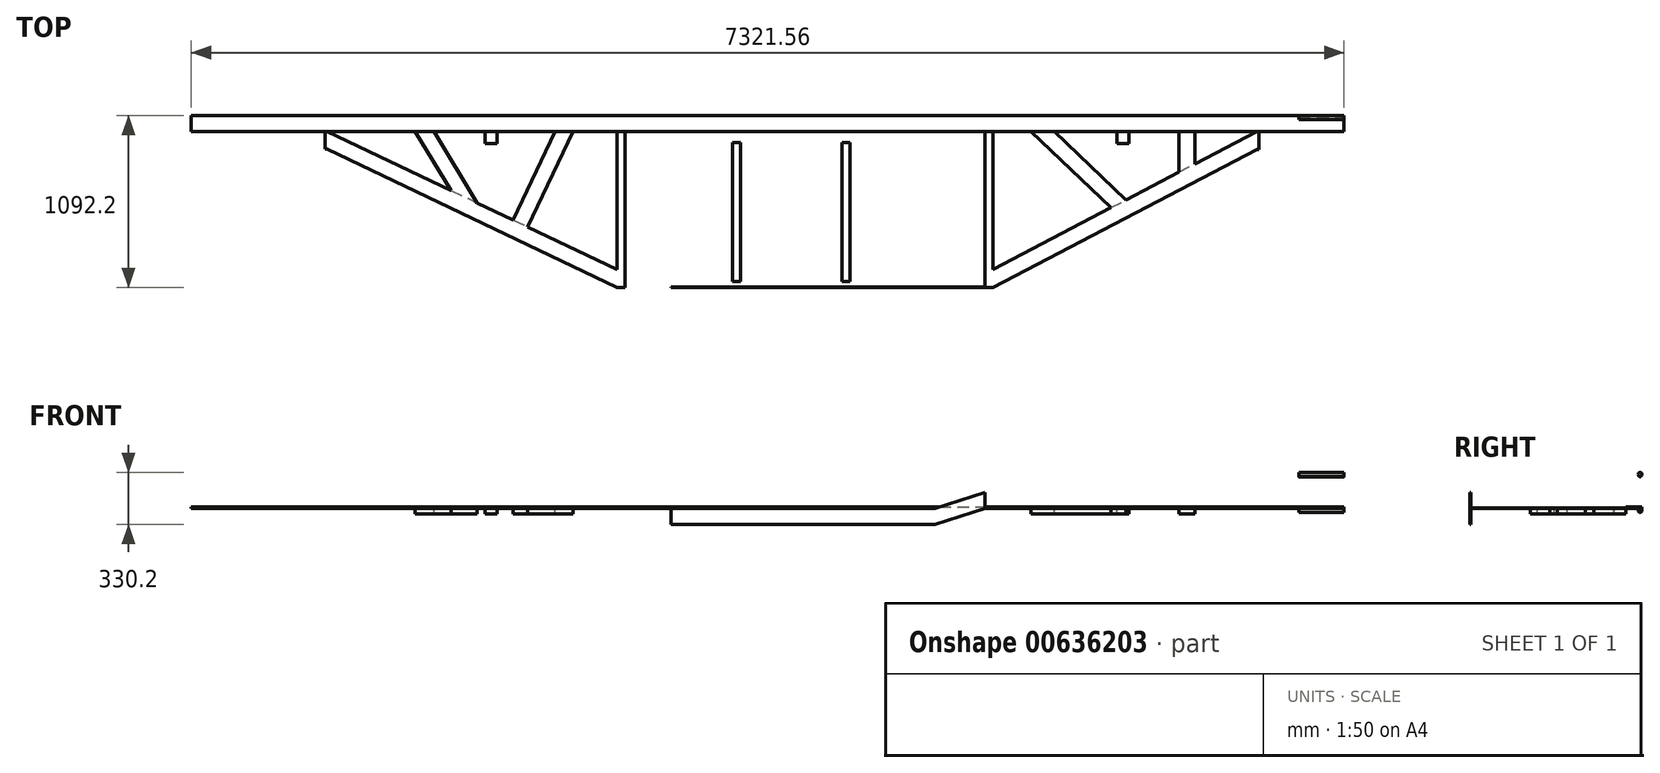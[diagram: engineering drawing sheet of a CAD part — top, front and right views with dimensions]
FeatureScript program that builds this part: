
annotation { "Feature Type Name" : "Feature", "Feature Type Description" : "" }
export const myFeature = defineFeature(function(context is Context, id is Id, definition is map)
    precondition{}
    {
        {
            assignVariable(context, id + "F0", {"name" : "MainRailLength", "anyValue" : 288.25});
        }
        {
            assignVariable(context, id + "F1", {"name" : "MainRailHeight", "anyValue" : 8});
        }
        {
            assignVariable(context, id + "F2", {"name" : "SideRailHeight", "anyValue" : 4});
        }
        {
            assignVariable(context, id + "F3", {"name" : "SideRailWidth", "anyValue" : 4});
        }
        {
            assignVariable(context, id + "F4", {"name" : "BunkRailHeight", "anyValue" : 4});
        }
        {
            var Q0;
            Q0=qCreatedBy(makeId("Top.planeOp"),FACE);
            var sketch = newSketch(context, id + "F5", { "sketchPlane" : qUnion([Q0])});
            skLineSegment(sketch, "E0.bottom", {"start": v(-3660.78, 0) * mm, "end": v(3660.78, 0) * mm});
            skLineSegment(sketch, "E0.top", {"start": v(-3660.78, -101.6) * mm, "end": v(3660.78, -101.6) * mm});
            skLineSegment(sketch, "E0.left", {"start": v(-3660.78, 0) * mm, "end": v(-3660.78, -101.6) * mm});
            skLineSegment(sketch, "E0.right", {"start": v(3660.78, 0) * mm, "end": v(3660.78, -101.6) * mm});
            skSolve(sketch);
        }
        {
            var Q0;
            Q0=makeQuery(id+"F5.imprint","IMPRINT",FACE,{"disambiguationData":[TD([[makeQuery(id+"F5.imprint","IMPRINT",EDGE,{"derivedFrom":sQuery(id+"F5.wireOp",EDGE,"E0.bottom")}),-1.0]])]});
            extrude(context, id + "F6", {"entities" : qUnion([Q0]), "depth" : (getVariable(context, 'MainRailHeight')) * mm, "offsetDistance" : 25.4 * mm});
        }
        {
            var Q0;
            Q0=makeQuery(id+"F6.opExtrude","SWEPT_FACE",FACE,{"disambiguationData":[OSD([sQuery(id+"F5.wireOp",EDGE,"E0.right")])]});
            var sketch = newSketch(context, id + "F7", { "sketchPlane" : qUnion([Q0])});
            skCircle(sketch, "E1", {"center": v(-12.7, 215.9) * mm, "radius": 12.7 * mm});
            skPoint(sketch, "E1.centerSnap0", {"position": v(-50.8, 203.2) * mm});
            skCircle(sketch, "E2", {"center": v(-12.7, -12.7) * mm, "radius": 12.7 * mm});
            skCircle(sketch, "E3", {"center": v(-12.7, 203.2) * mm, "radius": 3.18 * mm});
            skCircle(sketch, "E4", {"center": v(-12.7, 0) * mm, "radius": 3.18 * mm});
            skSolve(sketch);
        }
        {
            var Q0;
            {var subQ0=sQuery(id+"F7.wireOp",EDGE,"E3");var subQ1=sQuery(id+"F7.wireOp",EDGE,"E1");var subQ2=makeQuery(id+"F7.imprint","INTERSECT",VERTEX,{"disambiguationData":[OD(0.0)],"derivedFrom":[subQ1,subQ0]});Q0=makeQuery(id+"F7.imprint","IMPRINT",FACE,{"disambiguationData":[TD([[makeQuery(id+"F7.imprint","IMPRINT",EDGE,{"disambiguationData":[TD([[subQ2,1.0]])],"derivedFrom":subQ1}),1.0]])]});}
            var Q1;
            {var subQ0=sQuery(id+"F7.wireOp",EDGE,"E3");var subQ1=sQuery(id+"F7.wireOp",EDGE,"E1");var subQ2=makeQuery(id+"F7.imprint","INTERSECT",VERTEX,{"disambiguationData":[OD(0.0)],"derivedFrom":[subQ1,subQ0]});Q1=makeQuery(id+"F7.imprint","IMPRINT",FACE,{"disambiguationData":[TD([[makeQuery(id+"F7.imprint","IMPRINT",EDGE,{"disambiguationData":[TD([[subQ2,-1.0]])],"derivedFrom":subQ1}),-1.0]])]});}
            var Q2;
            {var subQ0=sQuery(id+"F7.wireOp",EDGE,"E3");var subQ1=sQuery(id+"F7.wireOp",EDGE,"E1");var subQ2=makeQuery(id+"F7.imprint","INTERSECT",VERTEX,{"disambiguationData":[OD(1.0)],"derivedFrom":[subQ1,subQ0]});Q2=makeQuery(id+"F7.imprint","IMPRINT",FACE,{"disambiguationData":[TD([[makeQuery(id+"F7.imprint","IMPRINT",EDGE,{"disambiguationData":[TD([[subQ2,1.0]])],"derivedFrom":subQ1}),-1.0]])]});}
            var Q3;
            {var subQ0=sQuery(id+"F7.wireOp",EDGE,"E3");var subQ1=makeQuery(id+"F6.opExtrude","CAP_EDGE",EDGE,{"disambiguationData":[OSD([sQuery(id+"F5.wireOp",EDGE,"E0.right")])],"isStart":false});var subQ2=makeQuery(id+"F7.imprint","INTERSECT",VERTEX,{"disambiguationData":[OD(0.0)],"derivedFrom":[subQ1,subQ0]});Q3=makeQuery(id+"F7.imprint","IMPRINT",FACE,{"disambiguationData":[TD([[makeQuery(id+"F7.imprint","IMPRINT",EDGE,{"disambiguationData":[TD([[subQ2,1.0]])],"derivedFrom":subQ0}),1.0]])]});}
            var Q4;
            {var subQ0=sQuery(id+"F7.wireOp",EDGE,"E3");var subQ1=sQuery(id+"F7.wireOp",EDGE,"E1");var subQ2=makeQuery(id+"F7.imprint","INTERSECT",VERTEX,{"disambiguationData":[OD(0.0)],"derivedFrom":[subQ1,subQ0]});Q4=makeQuery(id+"F7.imprint","IMPRINT",FACE,{"disambiguationData":[TD([[makeQuery(id+"F7.imprint","IMPRINT",EDGE,{"disambiguationData":[TD([[subQ2,-1.0]])],"derivedFrom":subQ1}),1.0]])]});}
            var Q5;
            {var subQ0=sQuery(id+"F7.wireOp",EDGE,"E4");var subQ1=sQuery(id+"F7.wireOp",EDGE,"E2");var subQ2=makeQuery(id+"F7.imprint","INTERSECT",VERTEX,{"disambiguationData":[OD(0.0)],"derivedFrom":[subQ1,subQ0]});Q5=makeQuery(id+"F7.imprint","IMPRINT",FACE,{"disambiguationData":[TD([[makeQuery(id+"F7.imprint","IMPRINT",EDGE,{"disambiguationData":[TD([[subQ2,1.0]])],"derivedFrom":subQ1}),1.0]])]});}
            var Q6;
            {var subQ0=sQuery(id+"F7.wireOp",EDGE,"E4");var subQ1=sQuery(id+"F7.wireOp",EDGE,"E2");var subQ2=makeQuery(id+"F7.imprint","INTERSECT",VERTEX,{"disambiguationData":[OD(0.0)],"derivedFrom":[subQ1,subQ0]});Q6=makeQuery(id+"F7.imprint","IMPRINT",FACE,{"disambiguationData":[TD([[makeQuery(id+"F7.imprint","IMPRINT",EDGE,{"disambiguationData":[TD([[subQ2,-1.0]])],"derivedFrom":subQ1}),1.0]])]});}
            var Q7;
            {var subQ0=sQuery(id+"F7.wireOp",EDGE,"E4");var subQ1=sQuery(id+"F7.wireOp",EDGE,"E2");var subQ2=makeQuery(id+"F7.imprint","INTERSECT",VERTEX,{"disambiguationData":[OD(1.0)],"derivedFrom":[subQ1,subQ0]});Q7=makeQuery(id+"F7.imprint","IMPRINT",FACE,{"disambiguationData":[TD([[makeQuery(id+"F7.imprint","IMPRINT",EDGE,{"disambiguationData":[TD([[subQ2,1.0]])],"derivedFrom":subQ1}),-1.0]])]});}
            var Q8;
            {var subQ0=sQuery(id+"F7.wireOp",EDGE,"E4");var subQ1=sQuery(id+"F7.wireOp",EDGE,"E2");var subQ2=makeQuery(id+"F7.imprint","INTERSECT",VERTEX,{"disambiguationData":[OD(0.0)],"derivedFrom":[subQ1,subQ0]});Q8=makeQuery(id+"F7.imprint","IMPRINT",FACE,{"disambiguationData":[TD([[makeQuery(id+"F7.imprint","IMPRINT",EDGE,{"disambiguationData":[TD([[subQ2,-1.0]])],"derivedFrom":subQ1}),-1.0]])]});}
            extrude(context, id + "F8", {"entities" : qUnion([Q0, Q1, Q2, Q3, Q4, Q5, Q6, Q7, Q8]), "operationType" : NewBodyOperationType.ADD, "oppositeDirection" : true, "depth" : (getVariable(context, 'MainRailLength')) * mm, "offsetDistance" : 25.4 * mm});
        }
        {
            var Q0;
            Q0=qCreatedBy(makeId("Top.planeOp"),FACE);
            var sketch = newSketch(context, id + "F9", { "sketchPlane" : qUnion([Q0])});
            skLineSegment(sketch, "E5.bottom", {"start": v(-955.67, -101.6) * mm, "end": v(-904.87, -101.6) * mm});
            skLineSegment(sketch, "E5.top", {"start": v(-955.67, -1092.2) * mm, "end": v(-904.87, -1092.2) * mm});
            skLineSegment(sketch, "E5.left", {"start": v(-955.67, -101.6) * mm, "end": v(-955.67, -1092.2) * mm});
            skLineSegment(sketch, "E5.right", {"start": v(-904.87, -101.6) * mm, "end": v(-904.87, -1092.2) * mm});
            skLineSegment(sketch, "E6.bottom", {"start": v(1381.12, -101.6) * mm, "end": v(1431.92, -101.6) * mm});
            skLineSegment(sketch, "E6.top", {"start": v(1381.12, -1092.2) * mm, "end": v(1431.93, -1092.2) * mm});
            skLineSegment(sketch, "E6.left", {"start": v(1381.12, -101.6) * mm, "end": v(1381.12, -1092.2) * mm});
            skLineSegment(sketch, "E6.right", {"start": v(1431.92, -101.6) * mm, "end": v(1431.92, -1092.2) * mm});
            skSolve(sketch);
        }
        {
            var Q0;
            Q0=makeQuery(id+"F9.imprint","IMPRINT",FACE,{"disambiguationData":[TD([[makeQuery(id+"F9.imprint","IMPRINT",EDGE,{"derivedFrom":sQuery(id+"F9.wireOp",EDGE,"E5.bottom")}),-1.0]])]});
            var Q1;
            Q1=makeQuery(id+"F9.imprint","IMPRINT",FACE,{"disambiguationData":[TD([[makeQuery(id+"F9.imprint","IMPRINT",EDGE,{"derivedFrom":sQuery(id+"F9.wireOp",EDGE,"E6.bottom")}),-1.0]])]});
            extrude(context, id + "F10", {"entities" : qUnion([Q0, Q1]), "operationType" : NewBodyOperationType.ADD, "depth" : (getVariable(context, 'BunkRailHeight')) * mm, "offsetDistance" : 25.4 * mm});
        }
        {
            var Q0;
            Q0=qCreatedBy(makeId("Top.planeOp"),FACE);
            var sketch = newSketch(context, id + "F11", { "sketchPlane" : qUnion([Q0])});
            skLineSegment(sketch, "E7.bottom", {"start": v(-222.25, -171.45) * mm, "end": v(-171.45, -171.45) * mm});
            skLineSegment(sketch, "E7.top", {"start": v(-222.25, -1054.1) * mm, "end": v(-171.45, -1054.1) * mm});
            skLineSegment(sketch, "E7.left", {"start": v(-222.25, -171.45) * mm, "end": v(-222.25, -1054.1) * mm});
            skLineSegment(sketch, "E7.right", {"start": v(-171.45, -171.45) * mm, "end": v(-171.45, -1054.1) * mm});
            skLineSegment(sketch, "E8.bottom", {"start": v(473.07, -171.45) * mm, "end": v(523.87, -171.45) * mm});
            skLineSegment(sketch, "E8.top", {"start": v(473.07, -1054.1) * mm, "end": v(523.87, -1054.1) * mm});
            skLineSegment(sketch, "E8.left", {"start": v(473.07, -171.45) * mm, "end": v(473.07, -1054.1) * mm});
            skLineSegment(sketch, "E8.right", {"start": v(523.87, -171.45) * mm, "end": v(523.87, -1054.1) * mm});
            skSolve(sketch);
        }
        {
            var Q0;
            Q0=makeQuery(id+"F11.imprint","IMPRINT",FACE,{"disambiguationData":[TD([[makeQuery(id+"F11.imprint","IMPRINT",EDGE,{"derivedFrom":sQuery(id+"F11.wireOp",EDGE,"E7.bottom")}),-1.0]])]});
            var Q1;
            Q1=makeQuery(id+"F11.imprint","IMPRINT",FACE,{"disambiguationData":[TD([[makeQuery(id+"F11.imprint","IMPRINT",EDGE,{"derivedFrom":sQuery(id+"F11.wireOp",EDGE,"E8.bottom")}),-1.0]])]});
            extrude(context, id + "F12", {"entities" : qUnion([Q0, Q1]), "depth" : (getVariable(context, 'BunkRailHeight')) * mm, "offsetDistance" : 25.4 * mm});
        }
        {
            var Q0;
            Q0=qCreatedBy(makeId("Top.planeOp"),FACE);
            var sketch = newSketch(context, id + "F13", { "sketchPlane" : qUnion([Q0])});
            skLineSegment(sketch, "E9", {"start": v(-2797.18, -101.6) * mm, "end": v(-955.67, -979.64) * mm});
            skLineSegment(sketch, "E10", {"start": v(1431.92, -977.57) * mm, "end": v(3108.33, -101.6) * mm});
            skLineSegment(sketch, "E11.0", {"start": v(-2797.18, -214.16) * mm, "end": v(-955.67, -1092.2) * mm});
            skLineSegment(sketch, "E12.0", {"start": v(1431.92, -1092.2) * mm, "end": v(3108.33, -216.23) * mm});
            skLineSegment(sketch, "E13", {"start": v(-955.67, -979.64) * mm, "end": v(-955.67, -1092.2) * mm});
            skLineSegment(sketch, "E14", {"start": v(1431.92, -977.57) * mm, "end": v(1431.92, -1092.2) * mm});
            skLineSegment(sketch, "E15", {"start": v(-2797.18, -214.16) * mm, "end": v(-2809.88, -214.16) * mm});
            skLineSegment(sketch, "E16", {"start": v(-2809.88, -214.16) * mm, "end": v(-2809.88, -101.6) * mm});
            skLineSegment(sketch, "E17", {"start": v(-2809.88, -101.6) * mm, "end": v(-2797.18, -101.6) * mm});
            skLineSegment(sketch, "E18", {"start": v(3108.33, -216.23) * mm, "end": v(3121.03, -216.23) * mm});
            skLineSegment(sketch, "E19", {"start": v(3121.03, -216.23) * mm, "end": v(3121.03, -101.6) * mm});
            skLineSegment(sketch, "E20", {"start": v(3121.03, -101.6) * mm, "end": v(3108.33, -101.6) * mm});
            skSolve(sketch);
        }
        {
            var Q0;
            Q0=makeQuery(id+"F13.imprint","IMPRINT",FACE,{"disambiguationData":[TD([[makeQuery(id+"F13.imprint","IMPRINT",EDGE,{"derivedFrom":sQuery(id+"F13.wireOp",EDGE,"E9")}),-1.0]])]});
            var Q1;
            Q1=makeQuery(id+"F13.imprint","IMPRINT",FACE,{"disambiguationData":[TD([[makeQuery(id+"F13.imprint","IMPRINT",EDGE,{"derivedFrom":sQuery(id+"F13.wireOp",EDGE,"E10")}),-1.0]])]});
            extrude(context, id + "F14", {"entities" : qUnion([Q0, Q1]), "operationType" : NewBodyOperationType.ADD, "depth" : (getVariable(context, 'SideRailHeight')) * mm, "offsetDistance" : 25.4 * mm});
        }
        {
            var Q0;
            Q0=makeQuery(id+"F10.opExtrude","SWEPT_FACE",FACE,{"disambiguationData":[OSD([sQuery(id+"F9.wireOp",EDGE,"E5.top")])]});
            var sketch = newSketch(context, id + "F15", { "sketchPlane" : qUnion([Q0])});
            skLineSegment(sketch, "E21.bottom", {"start": v(-612.77, 0) * mm, "end": v(1063.62, 0) * mm});
            skLineSegment(sketch, "E21.top", {"start": v(-612.77, -101.6) * mm, "end": v(1063.62, -101.6) * mm});
            skLineSegment(sketch, "E21.left", {"start": v(-612.78, 0) * mm, "end": v(-612.78, -101.6) * mm});
            skLineSegment(sketch, "E21.right", {"start": v(1063.62, 0) * mm, "end": v(1063.62, -101.6) * mm});
            skLineSegment(sketch, "E22", {"start": v(-612.78, 0) * mm, "end": v(-904.87, 101.6) * mm});
            skLineSegment(sketch, "E23", {"start": v(-904.87, 0) * mm, "end": v(-612.78, -101.6) * mm});
            skLineSegment(sketch, "E24.0", {"start": v(1381.12, 101.6) * mm, "end": v(1381.12, 0) * mm});
            skLineSegment(sketch, "E25", {"start": v(1381.12, 101.6) * mm, "end": v(1063.62, 0) * mm});
            skLineSegment(sketch, "E26", {"start": v(1381.12, 0) * mm, "end": v(1063.62, -101.6) * mm});
            skSolve(sketch);
        }
        {
            var Q0;
            Q0=makeQuery(id+"F15.imprint","IMPRINT",FACE,{"disambiguationData":[TD([[makeQuery(id+"F15.imprint","IMPRINT",EDGE,{"derivedFrom":sQuery(id+"F15.wireOp",EDGE,"E21.left")}),-1.0]])]});
            var Q1;
            Q1=makeQuery(id+"F15.imprint","IMPRINT",FACE,{"disambiguationData":[TD([[makeQuery(id+"F15.imprint","IMPRINT",EDGE,{"derivedFrom":sQuery(id+"F15.wireOp",EDGE,"E21.bottom")}),-1.0]])]});
            var Q2;
            Q2=makeQuery(id+"F15.imprint","IMPRINT",FACE,{"disambiguationData":[TD([[makeQuery(id+"F15.imprint","IMPRINT",EDGE,{"derivedFrom":sQuery(id+"F15.wireOp",EDGE,"E21.right")}),1.0]])]});
            extrude(context, id + "F16", {"entities" : qUnion([Q0, Q1, Q2]), "operationType" : NewBodyOperationType.ADD, "oppositeDirection" : true, "depth" : (getVariable(context, 'SideRailWidth')) * mm, "offsetDistance" : 25.4 * mm});
        }
        {
            var Q0;
            Q0=makeQuery(id+"F14.boolean.opBoolean","MERGE",FACE,{"derivedFrom":[makeQuery(id+"F10.opExtrude","CAP_FACE",FACE,{"disambiguationData":[OSD([sQuery(id+"F9.wireOp",EDGE,"E5.bottom"),sQuery(id+"F9.wireOp",EDGE,"E5.top"),sQuery(id+"F9.wireOp",EDGE,"E5.left"),sQuery(id+"F9.wireOp",EDGE,"E5.right")])],"isStart":false}),makeQuery(id+"F14.opExtrude","CAP_FACE",FACE,{"disambiguationData":[OSD([sQuery(id+"F13.wireOp",EDGE,"E9"),sQuery(id+"F13.wireOp",EDGE,"E11.0"),sQuery(id+"F13.wireOp",EDGE,"E13"),sQuery(id+"F13.wireOp",EDGE,"E15"),sQuery(id+"F13.wireOp",EDGE,"E16"),sQuery(id+"F13.wireOp",EDGE,"E17")])],"isStart":false})]});
            var sketch = newSketch(context, id + "F17", { "sketchPlane" : qUnion([Q0])});
            skLineSegment(sketch, "E27.bottom", {"start": v(2613.03, -101.6) * mm, "end": v(2714.62, -101.6) * mm});
            skLineSegment(sketch, "E27.left", {"start": v(2613.03, -101.6) * mm, "end": v(2613.03, -360.4) * mm});
            skLineSegment(sketch, "E27.right", {"start": v(2714.62, -101.6) * mm, "end": v(2714.62, -307.32) * mm});
            skLineSegment(sketch, "E28", {"start": v(2613.03, -360.4) * mm, "end": v(2714.62, -307.32) * mm});
            skLineSegment(sketch, "E29", {"start": v(1820.45, -101.6) * mm, "end": v(2276.33, -536.34) * mm});
            skLineSegment(sketch, "E30", {"start": v(2276.33, -536.34) * mm, "end": v(2181.23, -586.04) * mm});
            skLineSegment(sketch, "E31", {"start": v(2181.23, -586.04) * mm, "end": v(1673.22, -101.6) * mm});
            skLineSegment(sketch, "E32", {"start": v(1673.22, -101.6) * mm, "end": v(1820.45, -101.6) * mm});
            skLineSegment(sketch, "E33.bottom", {"start": v(2219.32, -101.6) * mm, "end": v(2295.52, -101.6) * mm});
            skLineSegment(sketch, "E33.top", {"start": v(2219.32, -177.8) * mm, "end": v(2295.52, -177.8) * mm});
            skLineSegment(sketch, "E33.left", {"start": v(2219.32, -101.6) * mm, "end": v(2219.32, -177.8) * mm});
            skLineSegment(sketch, "E33.right", {"start": v(2295.52, -101.6) * mm, "end": v(2295.52, -177.8) * mm});
            skLineSegment(sketch, "E34", {"start": v(-2238.38, -101.6) * mm, "end": v(-2011.7, -476.12) * mm});
            skLineSegment(sketch, "E35", {"start": v(-2119.61, -101.6) * mm, "end": v(-1844.76, -555.72) * mm});
            skLineSegment(sketch, "E36", {"start": v(-2238.38, -101.6) * mm, "end": v(-2119.61, -101.6) * mm});
            skLineSegment(sketch, "E37", {"start": v(-2011.7, -476.12) * mm, "end": v(-1844.76, -555.72) * mm});
            skLineSegment(sketch, "E38", {"start": v(-1349.37, -101.6) * mm, "end": v(-1616.69, -664.47) * mm});
            skLineSegment(sketch, "E39", {"start": v(-1236.9, -101.6) * mm, "end": v(-1524.98, -708.2) * mm});
            skLineSegment(sketch, "E40", {"start": v(-1349.38, -101.6) * mm, "end": v(-1236.9, -101.6) * mm});
            skLineSegment(sketch, "E41", {"start": v(-1616.69, -664.47) * mm, "end": v(-1524.98, -708.2) * mm});
            skLineSegment(sketch, "E42.bottom", {"start": v(-1793.88, -101.44) * mm, "end": v(-1717.68, -101.44) * mm});
            skLineSegment(sketch, "E42.top", {"start": v(-1793.88, -177.64) * mm, "end": v(-1717.68, -177.64) * mm});
            skLineSegment(sketch, "E42.left", {"start": v(-1793.88, -101.44) * mm, "end": v(-1793.88, -177.64) * mm});
            skLineSegment(sketch, "E42.right", {"start": v(-1717.68, -101.44) * mm, "end": v(-1717.68, -177.64) * mm});
            skSolve(sketch);
        }
        {
            var Q0;
            Q0=makeQuery(id+"F17.imprint","IMPRINT",FACE,{"disambiguationData":[TD([[makeQuery(id+"F17.imprint","IMPRINT",EDGE,{"derivedFrom":sQuery(id+"F17.wireOp",EDGE,"E34")}),1.0]])]});
            var Q1;
            Q1=makeQuery(id+"F17.imprint","IMPRINT",FACE,{"disambiguationData":[TD([[makeQuery(id+"F17.imprint","IMPRINT",EDGE,{"derivedFrom":sQuery(id+"F17.wireOp",EDGE,"E42.bottom")}),-1.0]])]});
            var Q2;
            Q2=makeQuery(id+"F17.imprint","IMPRINT",FACE,{"disambiguationData":[TD([[makeQuery(id+"F17.imprint","IMPRINT",EDGE,{"derivedFrom":sQuery(id+"F17.wireOp",EDGE,"E38")}),1.0]])]});
            var Q3;
            Q3=makeQuery(id+"F17.imprint","IMPRINT",FACE,{"disambiguationData":[TD([[makeQuery(id+"F17.imprint","IMPRINT",EDGE,{"derivedFrom":sQuery(id+"F17.wireOp",EDGE,"E29")}),-1.0]])]});
            var Q4;
            Q4=makeQuery(id+"F17.imprint","IMPRINT",FACE,{"disambiguationData":[TD([[makeQuery(id+"F17.imprint","IMPRINT",EDGE,{"derivedFrom":sQuery(id+"F17.wireOp",EDGE,"E33.bottom")}),-1.0]])]});
            var Q5;
            Q5=makeQuery(id+"F17.imprint","IMPRINT",FACE,{"disambiguationData":[TD([[makeQuery(id+"F17.imprint","IMPRINT",EDGE,{"derivedFrom":sQuery(id+"F17.wireOp",EDGE,"E27.bottom")}),-1.0]])]});
            extrude(context, id + "F18", {"entities" : qUnion([Q0, Q1, Q2, Q3, Q4, Q5]), "operationType" : NewBodyOperationType.ADD, "oppositeDirection" : true, "depth" : 38.1 * mm, "offsetDistance" : 25.4 * mm});
        }
    });
